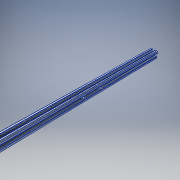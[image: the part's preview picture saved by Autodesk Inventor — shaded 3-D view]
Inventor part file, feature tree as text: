
AUTODESK INVENTOR PART (.ipt)
format: ipt  version: 2019 (Build 230136000, 136)  size: 528,896 bytes
history: native  units: in
note: dims shown in document units (in); Inventor stores cm internally (conversion verified against a paired STEP export)
features: extrude x3, sketch x3, other x1, plane x1, projected_geometry x1
ambient origin geometry x8: Origin, YZ Plane, XZ Plane, XY Plane, X Axis, Y Axis, Z Axis, Center Point
bodies: Solid1 (feature_tree)
feature tree (9):
  other  "Boss-Extrude1"
  extrude  "Extrusion1"  Depth=0.4375in
  plane  "Work Plane1"
  extrude  "Extrusion5"  Depth=0.25in
  extrude  "Extrusion6"  Depth=1.0in TaperAngle=0.0deg
  sketch  "Sketch1"  dims[d0=8.0in d1=0.0in d11=0.4375in]
  projected_geometry  "Projected Loop1"
  sketch  "Sketch6"  dims[d12=2.125in d13=0.25in]
  sketch  "Sketch7"  dims[d14=3.0in d15=1.0in d16=0.0in d17=1.0in d18=0.0in]
